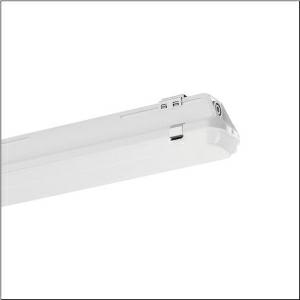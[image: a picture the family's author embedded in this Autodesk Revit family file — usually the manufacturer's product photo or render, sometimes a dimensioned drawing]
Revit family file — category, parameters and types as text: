
# Revit family: monsun_r__11_facade_51ff40mp360h_5056
name_source: partatom
category: Lighting Fixtures
units: mm (PartAtom-declared; Revit-internal decimal feet)

## family parameters
Cut with Voids When Loaded = No
Host = Face
Light Source = No
Part Type = Normal
Room Calculation Point = No
Round Connector Dimension = Use Diameter
Shared = No

## types (1)
- --- (1 x LED, 5790 lm, 33.6 W, 3000K)
    Apparent Load = 34 VA
    CIE Flux Codes = 47 77 93 95 100
    Color Rendering = 80
    Color Temperature = 3000K
    Default Elevation = 1800 mm
    Description = Monsun® 11 facade, damp-proof luminaire, chain hanger, primary optical cover: enclosure, of PMMA, light emission: direct distribution, primary light characteristic: symmetric, installation type: vertical mounting, horizontal mounting, surface-mounted, LED, rated luminous flux: 5.790lm, luminous efficacy: 172lm/W, light colour: 830, colour temperature: 3000K, control gear: ON/OFF Multilumen, with terminal, 3-pole, max. 2.5mm², mains connection: 220..240V, AC, 50/60Hz, rated input power: 34W, luminaire housing, of glass-fibre reinforced polyester, uncoated, bright grey, with climate membrane, for cables, Ø 8.4..12mm, incl. chain hanger, length: 1.590mm, width: 90mm, height: 88mm, clip for enclosure, of stainless steel (V2A), ceiling mounting element, of stainless steel (V2A), chain hanger, of stainless steel (V2A), protection rating (complete): IP66, insulation class (complete): insulation class I (protective earthing), certification: CE, ENEC, VDE, UKCA, protection symbol: D, impact resistance: IK06, permissible operating ambient temperature: -35..+50°C, standard: EN 60598-2-1, EN 50419, exposed outdoor area, contact your sales advisor before using the luminaires in applications with unclear chemical exposure, large temperature fluctuations or condensation-forming humidity, LABS conformity tested according to VDMA 24364:2018-05, packaging unit: 1 piece
    Height = 89 mm
    Lamp = 1 x LED
    Lamp Light Flux = 5790 lm
    Lamp Power = 33.6 W
    Lamp count = 1
    Length = 1590 mm
    Luminous efficacy = 172 lm/W
    Manufacturer = Siteco
    ModVariant = No
    Model = 51FF40MP360H
    Mounting Place = Ceiling
    Mounting Type = Surface mounted
    Number of Poles = 1
    OnlyDefault = Yes
    Power Factor = 1
    Product Name = Monsun® 11 facade
    Product group = damp-proof luminaire
    ProductGroupID = 300
    Protection Class = Protection class I
    Protection Degree = IP 66
    RLX_Detail_Level = 1
    RLX_Emergency_Light_Flux = 0 lm
    RLX_Emergency_Type = 0
    RLX_Emergency_Type_DB = No
    RlxData = <blob elided: 89709 chars, md5=8c33024b>
    Socket = socket
    Standby Power = 0 W
    System Light Flux = 5790 lm
    System Power = 34 W
    Type Comments = factory setting: luminous flux: 100 % | (A | C | E) | 77 mA
    Type Image = l_1349237.jpg
    URL = http://relux.com
    VarID = @adj_143338
    Voltage = 0 V
    Weight = 0.00 kg
    Width = 90 mm

## geometry (parser evidence)
native form markers: Blend x4, Sweep x12
no freeform markers — native parametric forms only
